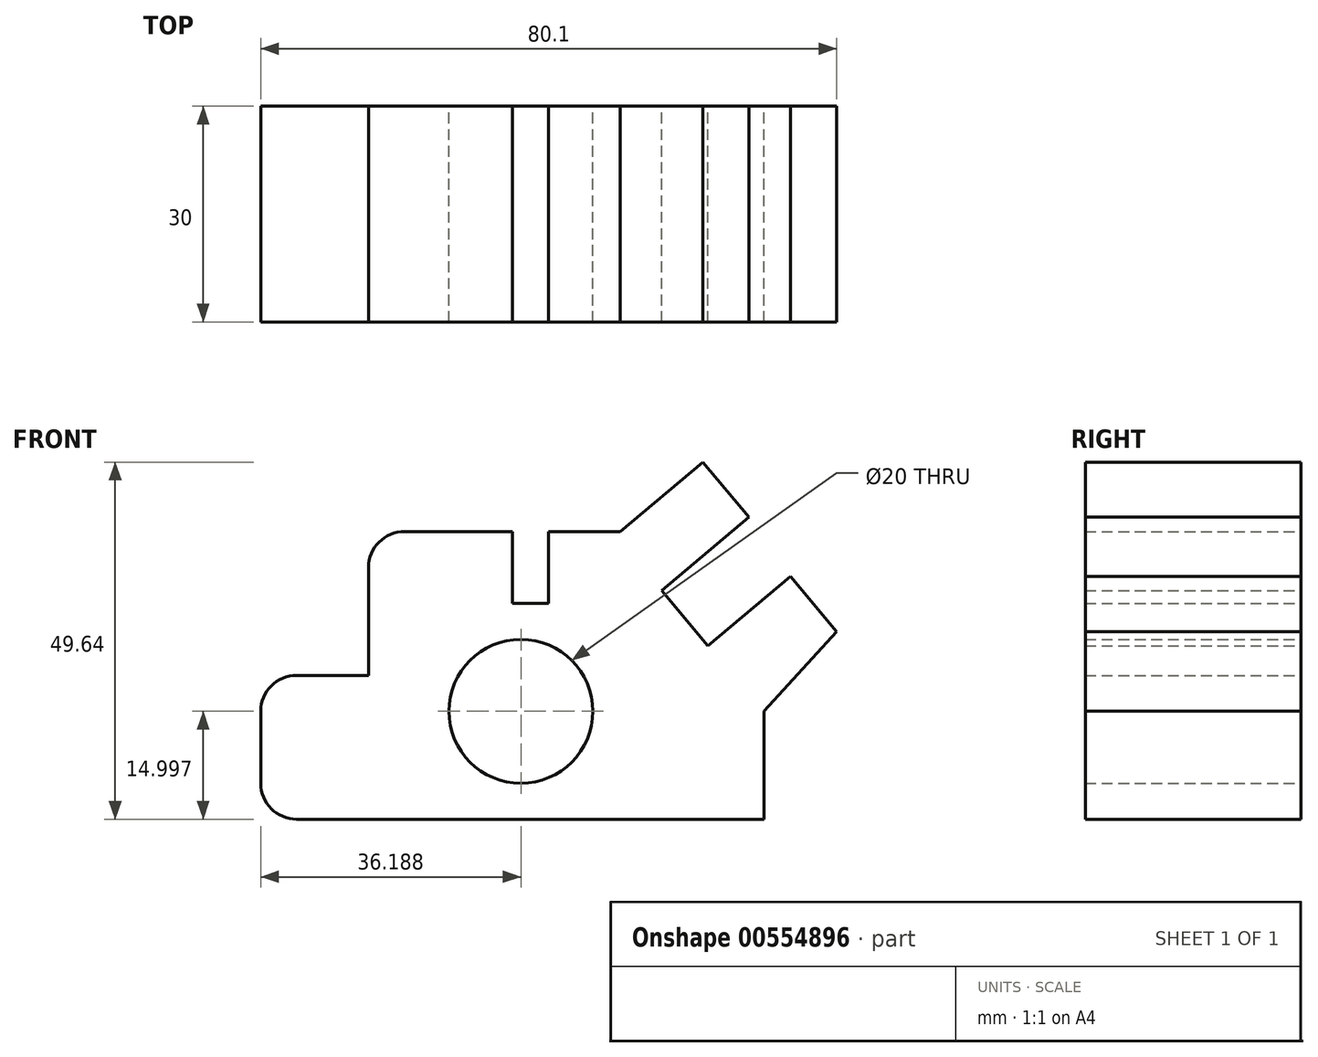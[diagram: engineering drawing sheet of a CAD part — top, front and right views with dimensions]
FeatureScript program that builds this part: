
annotation { "Feature Type Name" : "Feature", "Feature Type Description" : "" }
export const myFeature = defineFeature(function(context is Context, id is Id, definition is map)
    precondition{}
    {
        {
            var Q0;
            Q0=qCreatedBy(makeId("Front.planeOp"),FACE);
            var sketch = newSketch(context, id + "F0", { "sketchPlane" : qUnion([Q0])});
            skLineSegment(sketch, "E0", {"start": v(-33.38, -34.16) * mm, "end": v(31.62, -34.16) * mm});
            skLineSegment(sketch, "E1", {"start": v(-38.38, -29.16) * mm, "end": v(-38.38, -19.16) * mm});
            skLineSegment(sketch, "E2", {"start": v(31.62, -34.16) * mm, "end": v(31.62, -19.16) * mm});
            skLineSegment(sketch, "E3", {"start": v(-33.38, -14.16) * mm, "end": v(-23.38, -14.16) * mm});
            skLineSegment(sketch, "E4", {"start": v(-23.38, -14.16) * mm, "end": v(-23.38, 0.84) * mm});
            skPoint(sketch, "E5.visualSharp", {"position": v(-38.38, -34.16) * mm});
            skArc(sketch, "E5.filletArc", {"start": v(-38.38, -29.16) * mm, "mid": v(-36.91, -32.7) * mm, "end": v(-33.38, -34.16) * mm});
            skPoint(sketch, "E6.visualSharp", {"position": v(-38.38, -14.16) * mm});
            skArc(sketch, "E6.filletArc", {"start": v(-33.38, -14.16) * mm, "mid": v(-36.91, -15.63) * mm, "end": v(-38.38, -19.16) * mm});
            skLineSegment(sketch, "E7", {"start": v(-18.38, 5.84) * mm, "end": v(-3.38, 5.84) * mm});
            skPoint(sketch, "E8.visualSharp", {"position": v(-23.38, 5.84) * mm});
            skArc(sketch, "E8.filletArc", {"start": v(-18.38, 5.84) * mm, "mid": v(-21.91, 4.37) * mm, "end": v(-23.38, 0.84) * mm});
            skLineSegment(sketch, "E9", {"start": v(-3.38, 5.84) * mm, "end": v(-3.38, -4.16) * mm});
            skLineSegment(sketch, "E10", {"start": v(-3.38, -4.16) * mm, "end": v(1.62, -4.16) * mm});
            skLineSegment(sketch, "E11", {"start": v(1.62, -4.16) * mm, "end": v(1.62, 5.84) * mm});
            skLineSegment(sketch, "E12", {"start": v(1.62, 5.84) * mm, "end": v(11.62, 5.84) * mm});
            skLineSegment(sketch, "E13", {"start": v(11.62, 5.84) * mm, "end": v(23.11, 15.48) * mm});
            skLineSegment(sketch, "E14", {"start": v(23.11, 15.48) * mm, "end": v(29.54, 7.82) * mm});
            skLineSegment(sketch, "E15", {"start": v(29.54, 7.82) * mm, "end": v(17.37, -2.4) * mm});
            skLineSegment(sketch, "E16", {"start": v(17.37, -2.4) * mm, "end": v(23.8, -10.05) * mm});
            skLineSegment(sketch, "E17", {"start": v(23.8, -10.05) * mm, "end": v(35.3, -0.41) * mm});
            skLineSegment(sketch, "E18", {"start": v(35.3, -0.41) * mm, "end": v(41.72, -8.07) * mm});
            skLineSegment(sketch, "E19", {"start": v(31.62, -19.16) * mm, "end": v(41.72, -8.07) * mm});
            skCircle(sketch, "E20", {"center": v(-2.2, -19.16) * mm, "radius": 10 * mm});
            skSolve(sketch);
        }
        {
            var Q0;
            Q0 = qSketchRegion(id + "F0", true);
            extrude(context, id + "F1", {"entities" : qUnion([Q0]), "depth" : 30 * mm, "offsetDistance" : 25 * mm});
        }
    });
